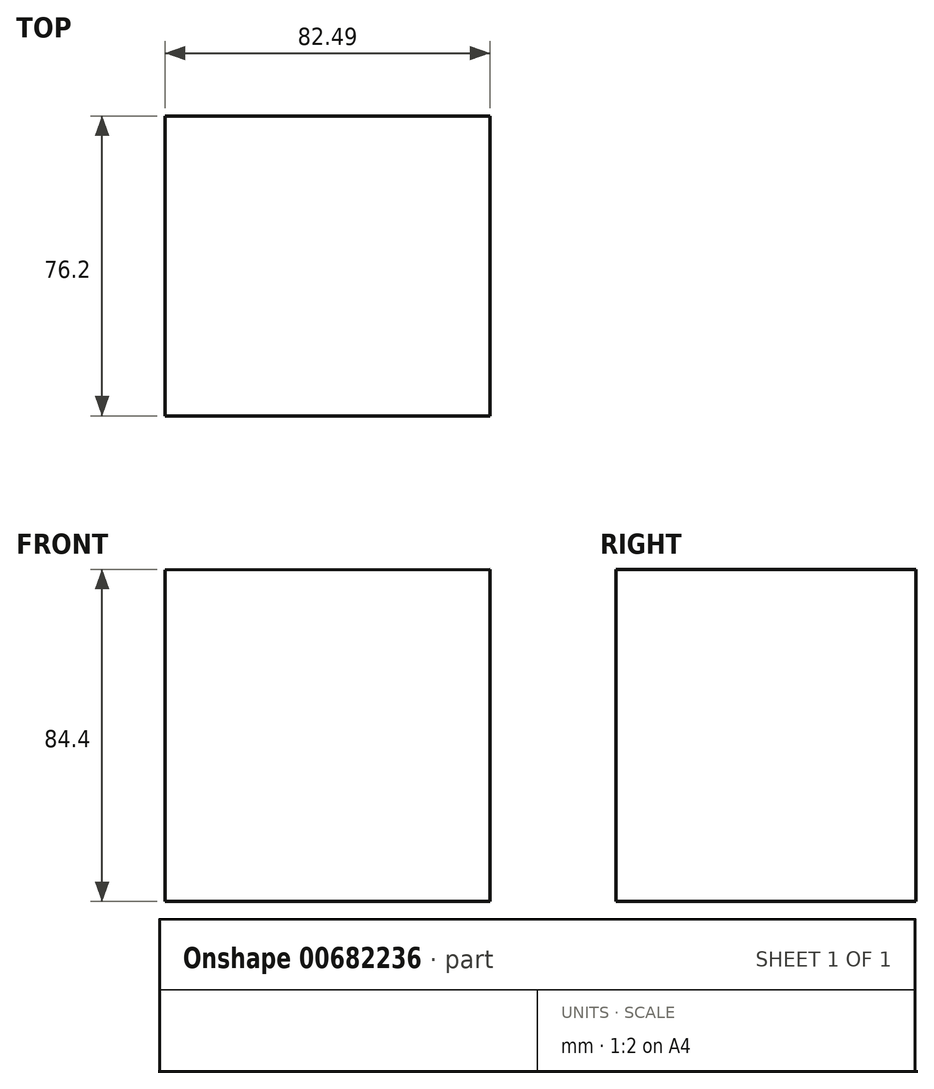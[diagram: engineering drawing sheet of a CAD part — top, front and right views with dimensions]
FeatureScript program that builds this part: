
annotation { "Feature Type Name" : "Feature", "Feature Type Description" : "" }
export const myFeature = defineFeature(function(context is Context, id is Id, definition is map)
    precondition{}
    {
        {
            var Q0;
            Q0=qCreatedBy(makeId("Front.planeOp"),FACE);
            var sketch = newSketch(context, id + "F0", { "sketchPlane" : qUnion([Q0])});
            skLineSegment(sketch, "E0", {"start": v(-53.75, 52.8) * mm, "end": v(-53.75, -31.41) * mm});
            skLineSegment(sketch, "E1", {"start": v(-53.75, -31.41) * mm, "end": v(28.74, -31.41) * mm});
            skLineSegment(sketch, "E2", {"start": v(28.74, -31.41) * mm, "end": v(28.74, 52.99) * mm});
            skLineSegment(sketch, "E3", {"start": v(28.74, 52.99) * mm, "end": v(-53.75, 52.8) * mm});
            skSolve(sketch);
        }
        {
            var Q0;
            Q0=makeQuery(id+"F0.imprint","IMPRINT",FACE,{"disambiguationData":[TD([[makeQuery(id+"F0.imprint","IMPRINT",EDGE,{"derivedFrom":sQuery(id+"F0.wireOp",EDGE,"E0")}),1.0]])]});
            extrude(context, id + "F1", {"entities" : qUnion([Q0]), "depth" : 76.2 * mm, "offsetDistance" : 25.4 * mm});
        }
    });
